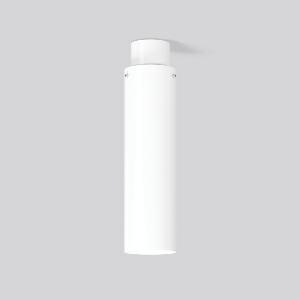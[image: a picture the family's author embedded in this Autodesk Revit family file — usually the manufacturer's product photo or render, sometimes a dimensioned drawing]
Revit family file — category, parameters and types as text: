
# Revit family: glasdownlight_931176_002_66dc
name_source: partatom
category: Lighting Fixtures
units: mm (PartAtom-declared; Revit-internal decimal feet)

## family parameters
Cut with Voids When Loaded = No
Host = Face
Light Source = No
Part Type = Normal
Room Calculation Point = No
Round Connector Dimension = Use Diameter
Shared = No

## types (1)
- GLASDOWNLIGHT (1 x LED Modul 830, 2400 lm, 3000)
    Apparent Load = 19 VA
    CIE Flux Codes = 16 41 69 51 100
    Color Rendering = 80
    Color Temperature = 3000
    Default Elevation = 1800 mm
    Description = Series: GLASDOWNLIGHT
Decorative round surface-mounted luminaire. Base: aluminium, powder-coated. Mouth blown 3-layer opal glass (Triplex glass) with satin finish. Glass fastening: retaining screws. Triplex glass produces particularly homogeneous, soft and glare free lighting. 
Colour: white
Diameter: 120 mm
Height: 470 mm
Lamp: LED
Socket: without socket
Colour temperature: 3000K
Colour rendering index (CRI): 80
System power: 19 W
Rated luminous flux: 2400 lm
Luminous efficiency: 126 lm/W
Control gear: Regulated power supply
Protection class: I
Type of protection: IP 20
    Height = 470 mm
    Lamp = 1 x LED Modul 830
    Lamp Light Flux = 2400 lm
    Lamp count = 1
    Length = 120 mm
    Lifetime = 50000 h
    Luminous efficacy = 126 lm/W
    Manufacturer = RZB
    ModVariant = No
    Model = 931176.002
    Mounting Place = Ceiling
    Mounting Type = Surface mounted
    Number of Poles = 1
    OnlyDefault = Yes
    Power Factor = 1
    Product Name = GLASDOWNLIGHT
    Product group = Surface mounted ceiling luminaires
    ProductGroupID = 303
    Protection Class = Protection class I
    Protection Degree = IP 20
    RLX_Detail_Level = 1
    RLX_Emergency_Light_Flux = 0 lm
    RLX_Emergency_Type = 0
    RLX_Emergency_Type_DB = No
    RlxData = <blob elided: 14273 chars, md5=03533485>
    Socket = socket
    Standby Power = 0 W
    System Light Flux = 2400 lm
    System Power = 19 W
    Type Comments = Product without accessories
    Type Image = 931176.002.jpg
    URL = http://relux.com
    VarID = ---
    Voltage = 230 V
    Voltage Range = 220-240 V
    Weight = 0.00 kg
    Width = 0 mm  [stored 0 ft]

note: [stored X ft] marks values corroborated as IEEE doubles in the binary element streams (Revit-internal decimal feet)

## geometry (parser evidence)
native form markers: Sweep x13
no freeform markers — native parametric forms only
